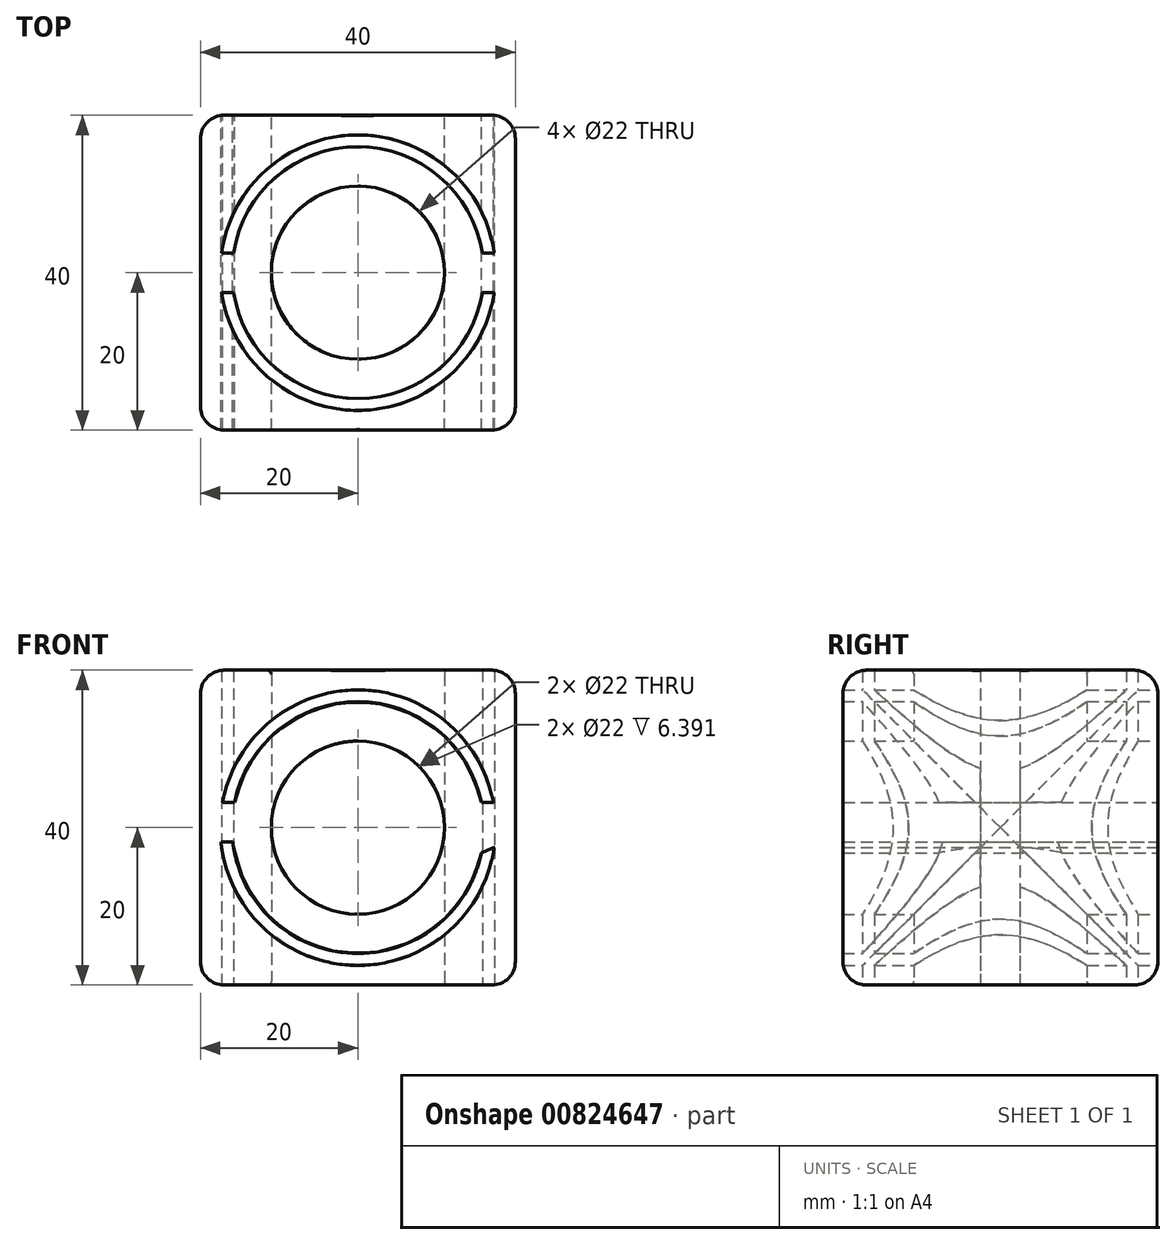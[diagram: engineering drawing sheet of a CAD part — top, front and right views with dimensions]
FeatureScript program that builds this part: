
annotation { "Feature Type Name" : "Feature", "Feature Type Description" : "" }
export const myFeature = defineFeature(function(context is Context, id is Id, definition is map)
    precondition{}
    {
        {
            var Q0;
            Q0=qCreatedBy(makeId("Top.planeOp"),FACE);
            var sketch = newSketch(context, id + "F0", { "sketchPlane" : qUnion([Q0])});
            skCircle(sketch, "E0", {"center": v(0, 0) * mm, "radius": 11 * mm});
            skLineSegment(sketch, "E1.top", {"start": v(0, -20) * mm, "end": v(20, -20) * mm});
            skLineSegment(sketch, "E1.right", {"start": v(20, 0) * mm, "end": v(20, -20) * mm});
            skLineSegment(sketch, "E2.MirrorCS", {"start": v(-20, 0) * mm, "end": v(-20, -20) * mm});
            skLineSegment(sketch, "E3.MirrorCS", {"start": v(0, -20) * mm, "end": v(-20, -20) * mm});
            skLineSegment(sketch, "E4.MirrorCS", {"start": v(20, 0) * mm, "end": v(20, 20) * mm});
            skLineSegment(sketch, "E5.MirrorCS", {"start": v(0, 20) * mm, "end": v(20, 20) * mm});
            skLineSegment(sketch, "E6.MirrorCS", {"start": v(0, 20) * mm, "end": v(-20, 20) * mm});
            skLineSegment(sketch, "E7.MirrorCS", {"start": v(-20, 0) * mm, "end": v(-20, 20) * mm});
            skArc(sketch, "E8", {"start": v(-15.8, -2.5) * mm, "mid": v(0, -16) * mm, "end": v(15.8, -2.5) * mm});
            skArc(sketch, "E9", {"start": v(-17.32, -2.5) * mm, "mid": v(0, -17.5) * mm, "end": v(17.32, -2.5) * mm});
            skLineSegment(sketch, "E10", {"start": v(-17.32, 2.5) * mm, "end": v(-15.8, 2.5) * mm});
            skLineSegment(sketch, "E11.MirrorCS", {"start": v(-17.32, -2.5) * mm, "end": v(-15.8, -2.5) * mm});
            skLineSegment(sketch, "E12.trimOffspring", {"start": v(15.8, 2.5) * mm, "end": v(17.32, 2.5) * mm});
            skLineSegment(sketch, "E13.trimOffspring", {"start": v(15.8, -2.5) * mm, "end": v(17.32, -2.5) * mm});
            skArc(sketch, "E14.trimOffspring", {"start": v(15.8, 2.5) * mm, "mid": v(0, 16) * mm, "end": v(-15.8, 2.5) * mm});
            skArc(sketch, "E15.trimOffspring", {"start": v(17.32, 2.5) * mm, "mid": v(0, 17.5) * mm, "end": v(-17.32, 2.5) * mm});
            skSolve(sketch);
        }
        {
            var Q0;
            Q0 = qSketchRegion(id + "F0", true);
            extrude(context, id + "F1", {"entities" : qUnion([Q0]), "depth" : 40 * mm, "offsetDistance" : 25 * mm});
        }
        {
            var Q0;
            Q0=makeQuery(id+"F1.opExtrude","SWEPT_FACE",FACE,{"disambiguationData":[OSD([sQuery(id+"F0.wireOp",EDGE,"E5.MirrorCS"),sQuery(id+"F0.wireOp",EDGE,"E6.MirrorCS")])]});
            var sketch = newSketch(context, id + "F2", { "sketchPlane" : qUnion([Q0])});
            skCircle(sketch, "E16", {"center": v(0, 20) * mm, "radius": 11 * mm});
            skArc(sketch, "E17", {"start": v(-15.68, 16.8) * mm, "mid": v(0.7, 4.02) * mm, "end": v(15.9, 18.2) * mm});
            skArc(sketch, "E18", {"start": v(-17.32, 17.5) * mm, "mid": v(0.35, 2.5) * mm, "end": v(17.4, 18.2) * mm});
            skLineSegment(sketch, "E19", {"start": v(-17.2, 23.2) * mm, "end": v(-15.68, 23.2) * mm});
            skPoint(sketch, "E20.start.orphan", {"position": v(0, 40) * mm});
            skPoint(sketch, "E21.orphan", {"position": v(-20, 20) * mm});
            skLineSegment(sketch, "E22.trimOffspring", {"start": v(15.68, 23.2) * mm, "end": v(17.2, 23.2) * mm});
            skArc(sketch, "E23.trimOffspring", {"start": v(15.68, 23.2) * mm, "mid": v(0, 36) * mm, "end": v(-15.68, 23.2) * mm});
            skArc(sketch, "E24.trimOffspring", {"start": v(17.2, 23.2) * mm, "mid": v(0, 37.5) * mm, "end": v(-17.2, 23.2) * mm});
            skPoint(sketch, "E25.orphan", {"position": v(20, 20) * mm});
            skLineSegment(sketch, "E26.MirrorCS", {"start": v(15.9, 18.2) * mm, "end": v(17.4, 18.2) * mm});
            skLineSegment(sketch, "E27.MirrorCS", {"start": v(-17.32, 17.5) * mm, "end": v(-15.68, 16.8) * mm});
            skSolve(sketch);
        }
        {
            var Q0;
            Q0 = qSketchRegion(id + "F2", true);
            extrude(context, id + "F3", {"entities" : qUnion([Q0]), "operationType" : NewBodyOperationType.REMOVE, "oppositeDirection" : true, "depth" : 40 * mm, "offsetDistance" : 25 * mm});
        }
        {
            var Q0;
            Q0=makeQuery(id+"F1.opExtrude","SWEPT_FACE",FACE,{"disambiguationData":[OSD([sQuery(id+"F0.wireOp",EDGE,"E2.MirrorCS"),sQuery(id+"F0.wireOp",EDGE,"E7.MirrorCS")])]});
            var sketch = newSketch(context, id + "F4", { "sketchPlane" : qUnion([Q0])});
            skCircle(sketch, "E28", {"center": v(0, 20) * mm, "radius": 11 * mm});
            skArc(sketch, "E29", {"start": v(-15.68, 16.8) * mm, "mid": v(0, 4) * mm, "end": v(15.68, 16.8) * mm});
            skArc(sketch, "E30", {"start": v(-17.32, 17.5) * mm, "mid": v(0, 2.5) * mm, "end": v(17.32, 17.5) * mm});
            skLineSegment(sketch, "E31", {"start": v(-17.2, 23.2) * mm, "end": v(-15.68, 23.2) * mm});
            skPoint(sketch, "E32.orphan", {"position": v(0, 40) * mm});
            skPoint(sketch, "E33.orphan", {"position": v(-20, 20) * mm});
            skLineSegment(sketch, "E34.trimOffspring", {"start": v(15.68, 23.2) * mm, "end": v(17.2, 23.2) * mm});
            skArc(sketch, "E35.trimOffspring", {"start": v(15.68, 23.2) * mm, "mid": v(0, 36) * mm, "end": v(-15.68, 23.2) * mm});
            skArc(sketch, "E36.trimOffspring", {"start": v(17.2, 23.2) * mm, "mid": v(0, 37.5) * mm, "end": v(-17.2, 23.2) * mm});
            skPoint(sketch, "E37.trimOffspring.end.orphan", {"position": v(0, 0) * mm});
            skPoint(sketch, "E38.orphan", {"position": v(20, 20) * mm});
            skLineSegment(sketch, "E39.MirrorCS", {"start": v(15.68, 16.8) * mm, "end": v(17.32, 17.5) * mm});
            skLineSegment(sketch, "E40.MirrorCS", {"start": v(-17.32, 17.5) * mm, "end": v(-15.68, 16.8) * mm});
            skSolve(sketch);
        }
        {
            var Q0;
            Q0=makeQuery(id+"F1.opExtrude","CAP_EDGE",EDGE,{"disambiguationData":[OSD([sQuery(id+"F0.wireOp",EDGE,"E5.MirrorCS"),sQuery(id+"F0.wireOp",EDGE,"E6.MirrorCS")])],"isStart":true});
            var Q1;
            Q1=makeQuery(id+"F1.opExtrude","CAP_EDGE",EDGE,{"disambiguationData":[OSD([sQuery(id+"F0.wireOp",EDGE,"E2.MirrorCS"),sQuery(id+"F0.wireOp",EDGE,"E7.MirrorCS")])],"isStart":true});
            var Q2;
            Q2=makeQuery(id+"F1.opExtrude","SWEPT_EDGE",EDGE,{"disambiguationData":[OSD([sQuery(id+"F0.wireOp",EDGE,"E6.MirrorCS"),sQuery(id+"F0.wireOp",EDGE,"E7.MirrorCS")])]});
            var Q3;
            Q3=makeQuery(id+"F1.opExtrude","SWEPT_EDGE",EDGE,{"disambiguationData":[OSD([sQuery(id+"F0.wireOp",EDGE,"E2.MirrorCS"),sQuery(id+"F0.wireOp",EDGE,"E3.MirrorCS")])]});
            var Q4;
            Q4=makeQuery(id+"F1.opExtrude","CAP_EDGE",EDGE,{"disambiguationData":[OSD([sQuery(id+"F0.wireOp",EDGE,"E1.top"),sQuery(id+"F0.wireOp",EDGE,"E3.MirrorCS")])],"isStart":true});
            var Q5;
            Q5=makeQuery(id+"F1.opExtrude","CAP_EDGE",EDGE,{"disambiguationData":[OSD([sQuery(id+"F0.wireOp",EDGE,"E2.MirrorCS"),sQuery(id+"F0.wireOp",EDGE,"E7.MirrorCS")])],"isStart":false});
            var Q6;
            Q6=makeQuery(id+"F1.opExtrude","SWEPT_EDGE",EDGE,{"disambiguationData":[OSD([sQuery(id+"F0.wireOp",EDGE,"E1.top"),sQuery(id+"F0.wireOp",EDGE,"E1.right")])]});
            var Q7;
            Q7=makeQuery(id+"F1.opExtrude","CAP_EDGE",EDGE,{"disambiguationData":[OSD([sQuery(id+"F0.wireOp",EDGE,"E1.top"),sQuery(id+"F0.wireOp",EDGE,"E3.MirrorCS")])],"isStart":false});
            var Q8;
            Q8=makeQuery(id+"F1.opExtrude","CAP_EDGE",EDGE,{"disambiguationData":[OSD([sQuery(id+"F0.wireOp",EDGE,"E1.right"),sQuery(id+"F0.wireOp",EDGE,"E4.MirrorCS")])],"isStart":false});
            var Q9;
            Q9=makeQuery(id+"F1.opExtrude","CAP_EDGE",EDGE,{"disambiguationData":[OSD([sQuery(id+"F0.wireOp",EDGE,"E5.MirrorCS"),sQuery(id+"F0.wireOp",EDGE,"E6.MirrorCS")])],"isStart":false});
            var Q10;
            Q10=makeQuery(id+"F1.opExtrude","SWEPT_EDGE",EDGE,{"disambiguationData":[OSD([sQuery(id+"F0.wireOp",EDGE,"E4.MirrorCS"),sQuery(id+"F0.wireOp",EDGE,"E5.MirrorCS")])]});
            var Q11;
            Q11=makeQuery(id+"F1.opExtrude","CAP_EDGE",EDGE,{"disambiguationData":[OSD([sQuery(id+"F0.wireOp",EDGE,"E1.right"),sQuery(id+"F0.wireOp",EDGE,"E4.MirrorCS")])],"isStart":true});
            fillet(context, id + "F5", {"entities" : qUnion([Q0, Q1, Q2, Q3, Q4, Q5, Q6, Q7, Q8, Q9, Q10, Q11]), "radius" : 3 * mm, "tangentPropagation" : true, "allowEdgeOverflow" : false});
        }
        {
            var Q0;
            Q0=makeQuery(id+"FiqRF7VeIfOyVCx_1.boolean.opBoolean","COPY",EDGE,{"derivedFrom":makeQuery(id+"FiqRF7VeIfOyVCx_1.opExtrude","CAP_EDGE",EDGE,{"disambiguationData":[OSD([sQuery(id+"F4.wireOp",EDGE,"E28")])],"isStart":false})});
            var Q1;
            Q1=makeQuery(id+"F3.boolean.opBoolean","COPY",EDGE,{"derivedFrom":makeQuery(id+"F3.opExtrude","CAP_EDGE",EDGE,{"disambiguationData":[OSD([sQuery(id+"F2.wireOp",EDGE,"E16")])],"isStart":true})});
            var Q2;
            Q2=makeQuery(id+"FiqRF7VeIfOyVCx_1.boolean.opBoolean","COPY",EDGE,{"derivedFrom":makeQuery(id+"FiqRF7VeIfOyVCx_1.opExtrude","CAP_EDGE",EDGE,{"disambiguationData":[OSD([sQuery(id+"F4.wireOp",EDGE,"E28")])],"isStart":true})});
            var Q3;
            Q3=makeQuery(id+"F3.boolean.opBoolean","COPY",EDGE,{"derivedFrom":makeQuery(id+"F3.opExtrude","CAP_EDGE",EDGE,{"disambiguationData":[OSD([sQuery(id+"F2.wireOp",EDGE,"E16")])],"isStart":false})});
            var Q4;
            Q4=makeQuery(id+"F1.opExtrude","CAP_EDGE",EDGE,{"disambiguationData":[OSD([sQuery(id+"F0.wireOp",EDGE,"E0")])],"isStart":true});
            var Q5;
            Q5=makeQuery(id+"F1.opExtrude","CAP_EDGE",EDGE,{"disambiguationData":[OSD([sQuery(id+"F0.wireOp",EDGE,"E0")])],"isStart":false});
            fillet(context, id + "F6", {"entities" : qUnion([Q0, Q1, Q2, Q3, Q4, Q5]), "radius" : 0.5 * mm, "tangentPropagation" : true, "allowEdgeOverflow" : false});
        }
    });
